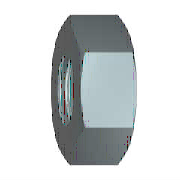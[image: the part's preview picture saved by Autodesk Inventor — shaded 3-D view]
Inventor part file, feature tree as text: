
AUTODESK INVENTOR PART (.ipt)
format: ipt  version: 2025.1 (Build 291241020, 241B)  size: 162,816 bytes
history: native  units: mm (DEFAULTED — no unit token found)
features: chamfer x1, hole x1, other x1, plane x1
ambient origin geometry x7: Origin, YZ Plane, XZ Plane, X Axis, Y Axis, Z Axis, Center Point
bodies: Solid1 (feature_tree), Body (feature_tree)
feature tree (4):
  chamfer  "Chamfer1"  Distance=27.712813mm
  hole  "Thread"  [1 undecoded]
  other  "Work Axis1"
  plane  "Work Plane1"
note: 1 required parameter value undecoded (feature->parameter linkage not recoverable at this tier; creation-order binding heuristic only, values carry confidence <= 0.55)
